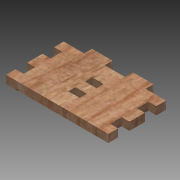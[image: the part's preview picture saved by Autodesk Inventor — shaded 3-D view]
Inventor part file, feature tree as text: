
AUTODESK INVENTOR PART (.ipt)
format: ipt  version: 2015 (Build 190159000, 159)  size: 257,536 bytes
history: native  units: mm
features: other x10, sketch x7, extrude x4
ambient origin geometry x8: Origin, YZ Plane, XZ Plane, XY Plane, X Axis, Y Axis, Z Axis, Center Point
bodies: Solid1 (feature_tree)
feature tree (21):
  other  "Blocks"
  extrude  "Extrusion1"  Depth=40.0mm
  sketch  "Sketch3"  dims[d2=5.5mm d3=0.0mm d16=5.5mm]
  extrude  "Extrusion4"  Depth=5.5mm
  extrude  "Extrusion5"  Depth=6.666667mm
  extrude  "Extrusion6"  Depth=5.0mm
  sketch  "Sketch16"  dims[d28=10.0mm d29=0.0mm]
  sketch  "Sketch17"  dims[d30=10.0mm d31=0.0mm d32=14.2mm d33=14.2mm d34=5.5mm d35=5.5mm d36=0.0mm]
  sketch  "Sketch15"  dims[d27=3.33mm]
  sketch  "Sketch1"  dims[d0=71.0mm d1=40.0mm]
  sketch  "Sketch4"  dims[d17=8.0mm d18=6.666667mm]
  sketch  "Sketch5"  dims[d25=8.0mm d26=5.0mm]
  other  "Block1"
  other  "Block2"
  other  "Block3"
  other  "Block4"
  other  "Block5"
  other  "Block4:1"
  other  "Block4:2"
  other  "Block5:1"
  other  "Block5:2"
